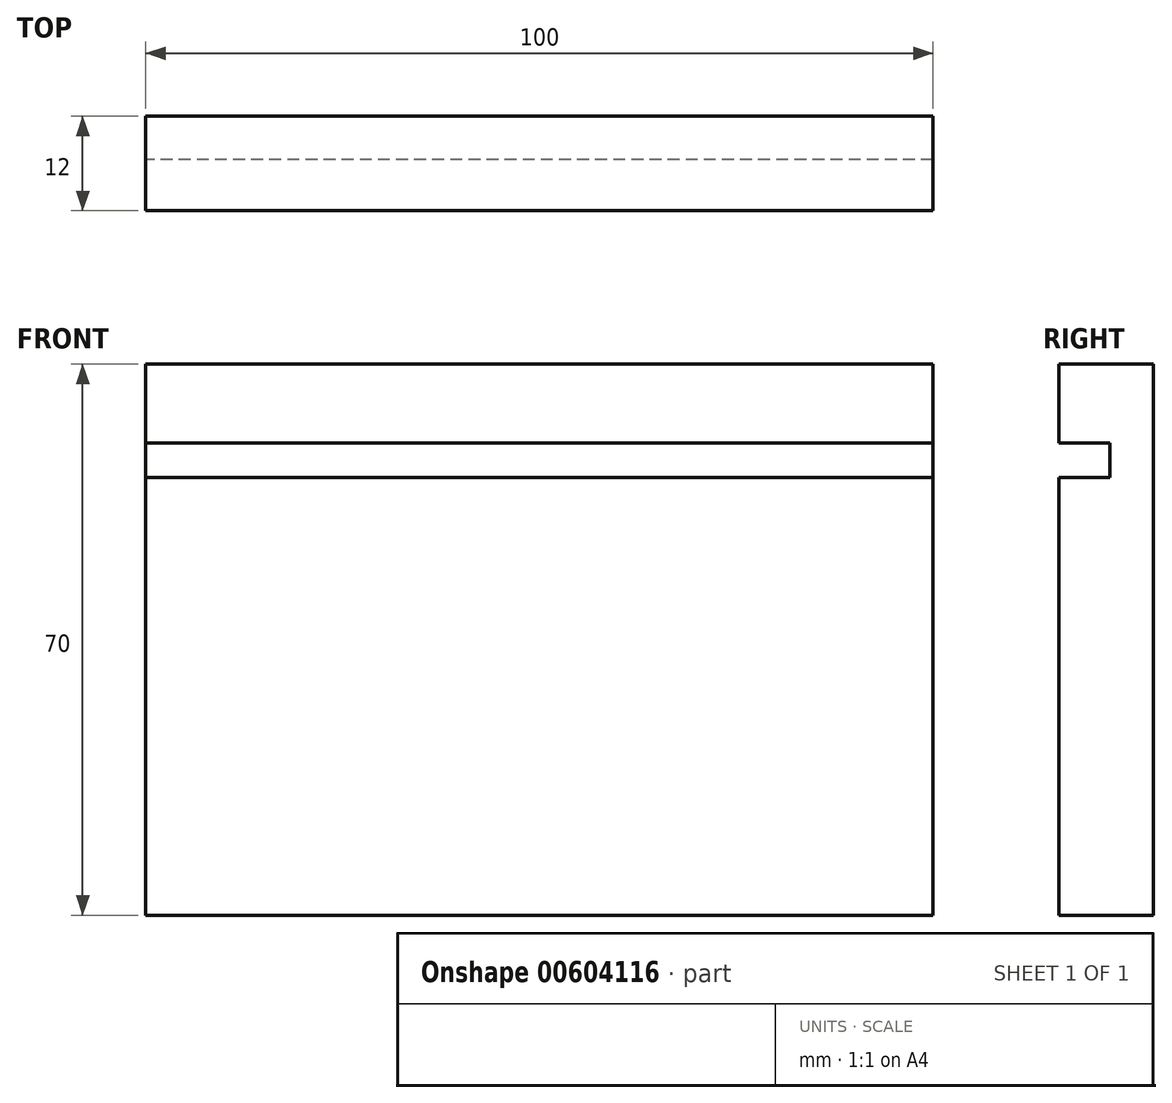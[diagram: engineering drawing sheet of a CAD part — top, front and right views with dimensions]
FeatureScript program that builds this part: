
annotation { "Feature Type Name" : "Feature", "Feature Type Description" : "" }
export const myFeature = defineFeature(function(context is Context, id is Id, definition is map)
    precondition{}
    {
        {
            var Q0;
            Q0=qCreatedBy(makeId("Right.planeOp"),FACE);
            var sketch = newSketch(context, id + "F0", { "sketchPlane" : qUnion([Q0])});
            skLineSegment(sketch, "E0", {"start": v(0, 0) * mm, "end": v(0, 70) * mm});
            skLineSegment(sketch, "E1", {"start": v(0, 70) * mm, "end": v(-12, 70) * mm});
            skLineSegment(sketch, "E2", {"start": v(-12, 70) * mm, "end": v(-12, 60) * mm});
            skLineSegment(sketch, "E3", {"start": v(-12, 60) * mm, "end": v(-5.53, 60) * mm});
            skLineSegment(sketch, "E4", {"start": v(-5.53, 60) * mm, "end": v(-5.53, 55.61) * mm});
            skLineSegment(sketch, "E5", {"start": v(-5.53, 55.61) * mm, "end": v(-12, 55.61) * mm});
            skLineSegment(sketch, "E6", {"start": v(-12, 55.61) * mm, "end": v(-12, 0) * mm});
            skLineSegment(sketch, "E7", {"start": v(-12, 0) * mm, "end": v(0, 0) * mm});
            skSolve(sketch);
        }
        {
            var Q0;
            Q0 = qSketchRegion(id + "F0", true);
            extrude(context, id + "F1", {"entities" : qUnion([Q0]), "depth" : 100 * mm, "offsetDistance" : 25 * mm});
        }
    });
